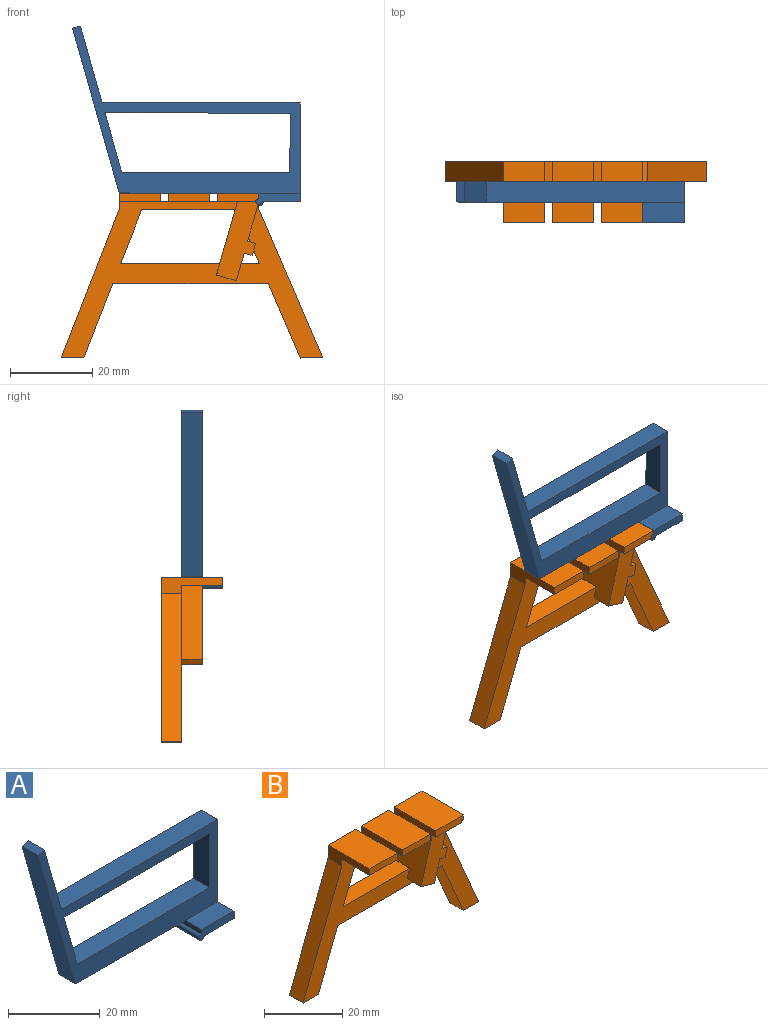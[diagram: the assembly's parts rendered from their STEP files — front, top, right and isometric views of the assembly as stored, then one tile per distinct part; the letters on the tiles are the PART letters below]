
ASSEMBLY  parts=2 mates=1
PART A: 17 faces, bbox 55.4x10x43.3 mm
  f0: plane 40.85x5mm, normal (0,0,1), area 204.2mm2, adj f1,f7,f9,f16
  f1: plane 14.5x5mm, normal (0.96,0,0.27), area 75.4mm2, adj f0,f7,f9,f15
  f2: plane 10x1.25mm, normal (-1,0,0), area 12.5mm2, adj f5,f6,f7,f8,f10
  f3: plane 10x9.25mm, normal (0,0,-1), area 92.5mm2, adj f4,f6,f7,f10
  f4: plane 24x10mm, normal (1,0,0), area 130mm2, adj f3,f5,f6,f7,f9,f14
  f5: plane 10x5mm, normal (0,0,1), area 50mm2, adj f2,f4,f6,f9
  f6: plane 10.75x2.75mm, normal (0,-1,0), area 21.3mm2, adj f2,f3,f4,f5,f10
  f7: plane 55.43x43.3mm, normal (0,1,0), area 474.1mm2, adj f0,f1,f2,f3,f4,f8,f10,f11
  f8: plane 34x5mm, normal (0,0,-1), area 170mm2, adj f2,f7,f9,f13
  f9: plane 55.43x40.55mm, normal (0,-1,0), area 452.8mm2, adj f0,f1,f4,f5,f8,f11,f12,f13
  f10: cylinder r=0.75mm len=10mm, axis (0,1,0), area 35.3mm2, adj f2,f3,f6,f7
  f11: plane 5x1.92mm, normal (-0.27,0,0.96), area 10mm2, adj f7,f9,f12,f13
  f12: plane 18.55x5.3mm, normal (0.96,0,0.27), area 96.5mm2, adj f7,f9,f11,f14
  f13: plane 40x11.43mm, normal (-0.96,0,-0.27), area 208mm2, adj f7,f8,f9,f11
  f14: plane 48.21x5mm, normal (0,0,1), area 241mm2, adj f4,f7,f9,f12
  f15: plane 44.99x5mm, normal (0,0,-1), area 225mm2, adj f1,f7,f9,f16
  f16: plane 14.5x5mm, normal (-1,0,0), area 72.5mm2, adj f0,f7,f9,f15
PART B: 45 faces, bbox 63.6x15x40 mm
  f0: plane 10x8.89mm, normal (0.96,0,-0.28), area 50.1mm2, adj f7,f8,f9,f38,f41,f43
  f1: plane 5x3.23mm, normal (-0.92,0,-0.4), area 17.6mm2, adj f6,f8,f9,f42
  f2: plane 15x1.25mm, normal (1,0,0), area 17.5mm2, adj f4,f8,f9,f26,f28,f41
  f3: plane 10x9.25mm, normal (0,0,-1), area 70.2mm2, adj f4,f8,f27,f38,f39,f41
  f4: plane 10x2mm, normal (0,-1,0), area 19.6mm2, adj f2,f3,f26,f27,f41
  f5: plane 10x6.73mm, normal (0.96,0,-0.28), area 48mm2, adj f6,f8,f9,f38,f40,f44
  f6: plane 5x4.41mm, normal (0,0,1), area 22mm2, adj f1,f5,f8,f9
  f7: plane 5x0.93mm, normal (-0.92,0,-0.4), area 5mm2, adj f0,f8,f9,f43
  f8: plane 63.55x39mm, normal (0,-1,0), area 596.4mm2, adj f0,f1,f2,f3,f5,f6,f7,f10
  f9: plane 63.55x40mm, normal (0,1,0), area 758mm2, adj f0,f1,f2,f5,f6,f7,f10,f11
  f10: plane 5x1mm, normal (1,0,0), area 5mm2, adj f8,f9,f28,f34
  f11: plane 18x7.03mm, normal (0.93,0,-0.36), area 96.6mm2, adj f8,f9,f30,f31
  f12: plane 13x5.07mm, normal (0.93,0,-0.36), area 69.8mm2, adj f8,f9,f13,f32
  f13: plane 22.72x5mm, normal (0,0,-1), area 113.6mm2, adj f8,f9,f12,f39
  f14: plane 5x2mm, normal (0,0,1), area 10mm2, adj f8,f9,f24,f27
  f15: plane 5x2mm, normal (0,0,1), area 10mm2, adj f8,f9,f19,f23
  f16: plane 15x4mm, normal (-1,0,0), area 40mm2, adj f8,f9,f17,f18,f20,f29
  f17: plane 10x10mm, normal (0,0,-1), area 100mm2, adj f8,f16,f19,f20
  f18: plane 15x10mm, normal (0,0,1), area 150mm2, adj f9,f16,f19,f20
  f19: plane 15x2mm, normal (1,0,0), area 30mm2, adj f9,f15,f17,f18,f20
  f20: plane 10x2mm, normal (0,-1,0), area 20mm2, adj f16,f17,f18,f19
  f21: plane 10x10mm, normal (0,0,-1), area 100mm2, adj f8,f23,f24,f25
  f22: plane 15x10mm, normal (0,0,1), area 150mm2, adj f9,f23,f24,f25
  f23: plane 15x2mm, normal (-1,0,0), area 30mm2, adj f9,f15,f21,f22,f25
  f24: plane 15x2mm, normal (1,0,0), area 30mm2, adj f9,f14,f21,f22,f25
  f25: plane 10x2mm, normal (0,-1,0), area 20mm2, adj f21,f22,f23,f24
  f26: plane 15x10mm, normal (0,0,1), area 150mm2, adj f2,f4,f9,f27
  f27: plane 15x2mm, normal (-1,0,0), area 30mm2, adj f3,f4,f9,f14,f26
  f28: cylinder r=1mm len=5mm, axis (0,1,0), area 15.7mm2, adj f2,f8,f9,f10
  f29: plane 36x14.05mm, normal (-0.93,0,0.36), area 193.2mm2, adj f8,f9,f16,f30
  f30: plane 5.5x5mm, normal (0,0,-1), area 27.5mm2, adj f8,f9,f11,f29
  f31: plane 5x0mm, normal (-1,0,0), area 0mm2, adj f8,f9,f11,f33
  f32: plane 24.06x5mm, normal (0,0,1), area 120.3mm2, adj f8,f9,f12,f39
  f33: plane 37.78x5mm, normal (0,0,-1), area 188.9mm2, adj f8,f9,f31,f35
  f34: plane 36x15.5mm, normal (0.92,0,0.4), area 196mm2, adj f8,f9,f10,f37
  f35: plane 18x7.75mm, normal (-0.92,0,-0.4), area 98mm2, adj f8,f9,f33,f36
  f36: plane 5x0mm, normal (1,0,0), area 0mm2, adj f8,f9,f35,f37
  f37: plane 5.5x5mm, normal (0,0,-1), area 27.5mm2, adj f8,f9,f34,f36
  f38: plane 19.22x10.12mm, normal (0,-1,0), area 102.1mm2, adj f0,f3,f5,f39,f40,f41,f42,f43
  f39: plane 17.84x10mm, normal (-0.96,0,0.28), area 160.4mm2, adj f3,f8,f9,f13,f32,f38,f40
  f40: plane 5x4.81mm, normal (-0.28,0,-0.96), area 25mm2, adj f5,f8,f38,f39
  f41: cylinder r=0.75mm len=15mm, axis (0,1,0), area 40.2mm2, adj f0,f2,f3,f4,f8,f9,f38
  f42: plane 10x2.88mm, normal (0.96,0,-0.28), area 21.6mm2, adj f1,f8,f9,f38,f43,f44
  f43: plane 10x1.93mm, normal (0.28,0,0.96), area 13.3mm2, adj f0,f7,f8,f9,f38,f42
  f44: plane 10x1.93mm, normal (-0.28,0,-0.96), area 20.1mm2, adj f5,f9,f38,f42
PLACE A rot(axis=(0,1,0),0.2deg) t=(0,-5,0.05)mm
PLACE B at identity fixed
MATE revolute B.f41 <-> A.f10  axis (0,-1,0) through (17,-5,0)mm
